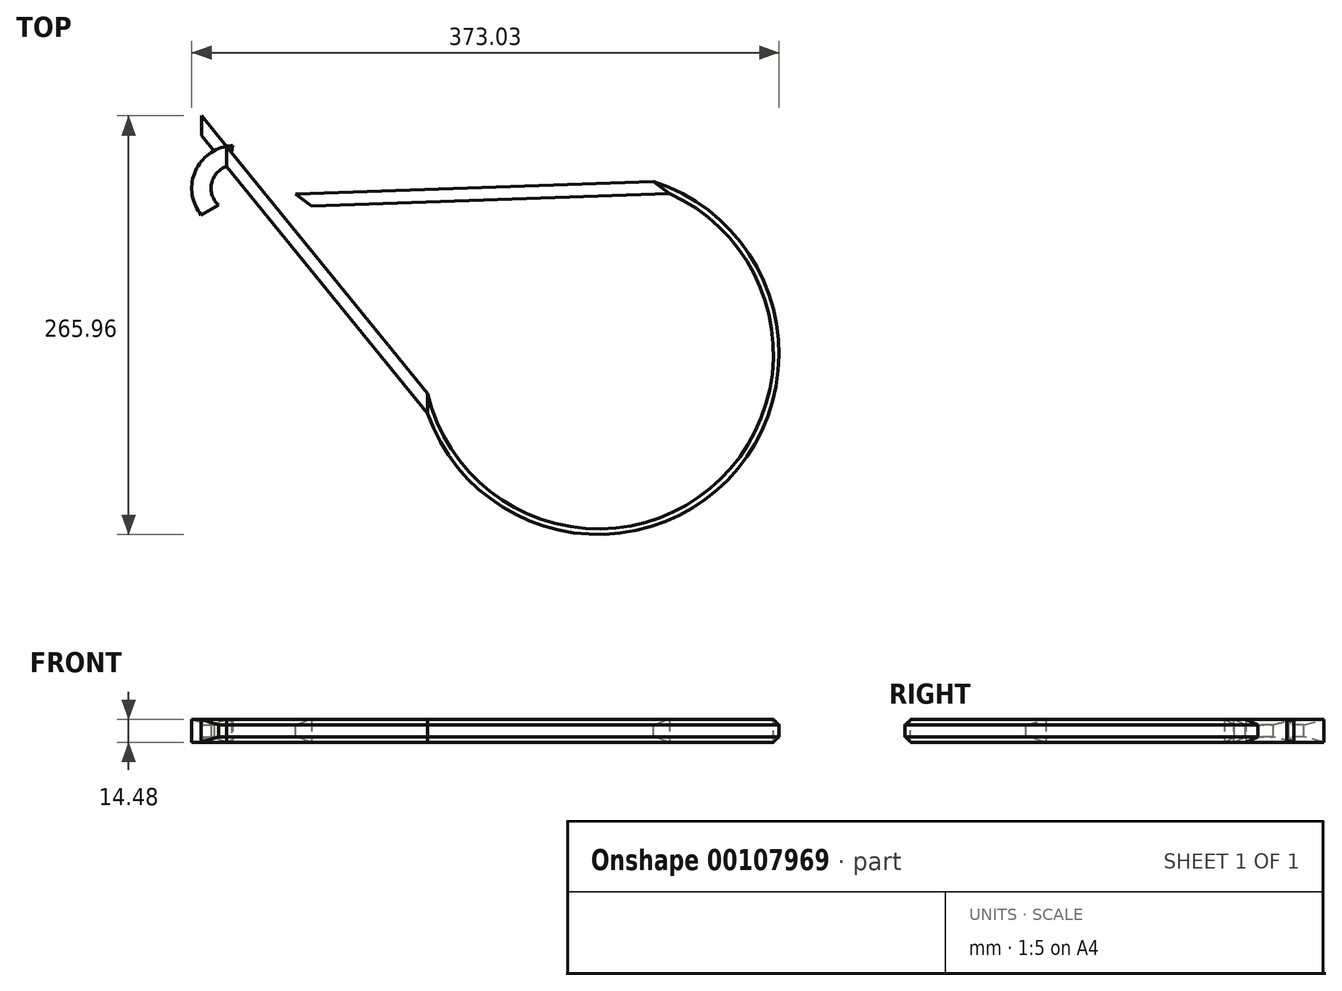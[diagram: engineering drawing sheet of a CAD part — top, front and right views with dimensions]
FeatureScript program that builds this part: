
annotation { "Feature Type Name" : "Feature", "Feature Type Description" : "" }
export const myFeature = defineFeature(function(context is Context, id is Id, definition is map)
    precondition{}
    {
        {
            var Q0;
            Q0=qCreatedBy(makeId("Top.planeOp"),FACE);
            var sketch = newSketch(context, id + "F0", { "sketchPlane" : qUnion([Q0])});
            skArc(sketch, "E0", {"start": v(3.9, 19.82) * mm, "mid": v(-19.46, 4.2) * mm, "end": v(-15.87, -23.67) * mm});
            skArc(sketch, "E1", {"start": v(127.7, -200.1) * mm, "mid": v(363.24, -169.73) * mm, "end": v(231.22, 27.69) * mm});
            skLineSegment(sketch, "E2", {"start": v(3.9, 19.82) * mm, "end": v(231.22, 27.69) * mm});
            skLineSegment(sketch, "E3", {"start": v(-15.87, -23.67) * mm, "end": v(127.7, -200.1) * mm});
            skSolve(sketch);
        }
        {
            var Q0;
            Q0=qCreatedBy(makeId("Right.planeOp"),FACE);
            var sketch = newSketch(context, id + "F1", { "sketchPlane" : qUnion([Q0])});
            skLineSegment(sketch, "E4", {"start": v(19.68, 0) * mm, "end": v(19.68, -14.48) * mm});
            skLineSegment(sketch, "E5", {"start": v(19.68, -14.48) * mm, "end": v(6.98, -11.08) * mm});
            skLineSegment(sketch, "E6", {"start": v(6.98, -11.08) * mm, "end": v(6.98, -3.4) * mm});
            skLineSegment(sketch, "E7", {"start": v(6.98, -3.4) * mm, "end": v(19.68, 0) * mm});
            skLineSegment(sketch, "E8", {"start": v(19.68, -7.24) * mm, "end": v(4.2, -7.24) * mm, "construction": true});
            skSolve(sketch);
        }
        {
            var Q0;
            Q0=makeQuery(id+"F1.imprint","IMPRINT",FACE,{"disambiguationData":[TD([[makeQuery(id+"F1.imprint","IMPRINT",EDGE,{"derivedFrom":sQuery(id+"F1.wireOp",EDGE,"E4")}),-1.0]])]});
            var Q1;
            Q1=sQuery(id+"F0.wireOp",EDGE,"E2");
            var Q2;
            Q2=sQuery(id+"F0.wireOp",EDGE,"E1");
            var Q3;
            Q3=sQuery(id+"F0.wireOp",EDGE,"E3");
            sweep(context, id + "F2", {"profiles" : qUnion([Q0]), "path" : qUnion([Q1, Q2, Q3])});
        }
        {
            var Q0;
            Q0=makeQuery(id+"F1.imprint","IMPRINT",FACE,{"disambiguationData":[TD([[makeQuery(id+"F1.imprint","IMPRINT",EDGE,{"derivedFrom":sQuery(id+"F1.wireOp",EDGE,"E4")}),-1.0]])]});
            var Q1;
            Q1=sQuery(id+"F0.wireOp",EDGE,"E0");
            sweep(context, id + "F3", {"operationType" : NewBodyOperationType.ADD, "profiles" : qUnion([Q0]), "path" : qUnion([Q1])});
        }
    });
